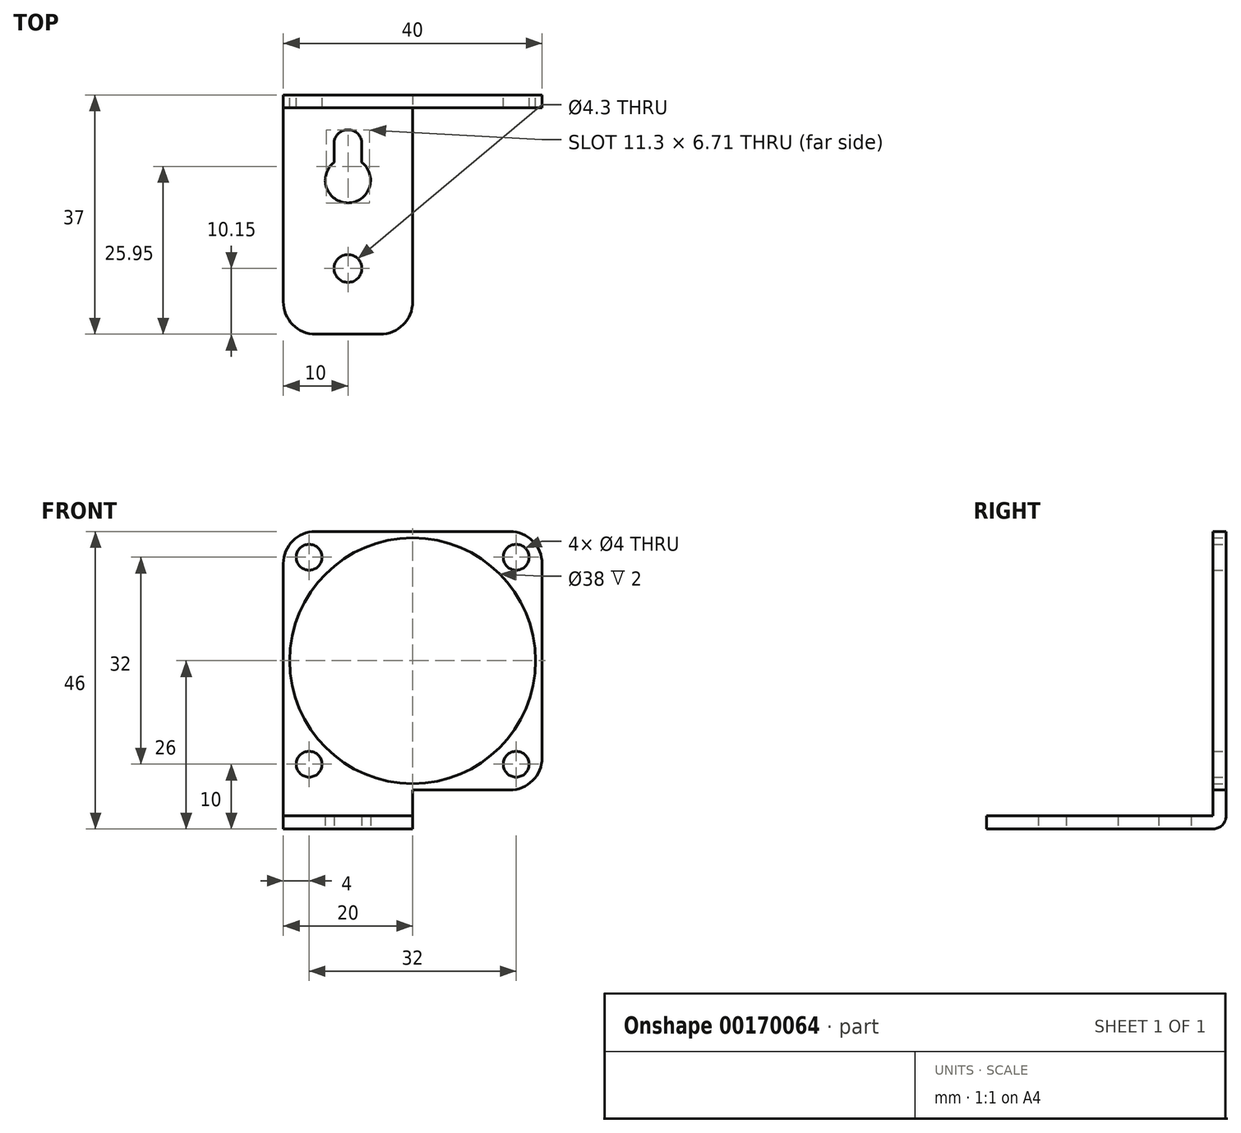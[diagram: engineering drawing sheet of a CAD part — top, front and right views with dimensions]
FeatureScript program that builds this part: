
annotation { "Feature Type Name" : "Feature", "Feature Type Description" : "" }
export const myFeature = defineFeature(function(context is Context, id is Id, definition is map)
    precondition{}
    {
        {
            var Q0;
            Q0=qCreatedBy(makeId("Front.planeOp"),FACE);
            var sketch = newSketch(context, id + "F0", { "sketchPlane" : qUnion([Q0])});
            skLineSegment(sketch, "E0.bottom", {"start": v(20, -20) * mm, "end": v(-20, -20) * mm});
            skLineSegment(sketch, "E0.top", {"start": v(20, 20) * mm, "end": v(-20, 20) * mm});
            skLineSegment(sketch, "E0.left", {"start": v(20, -20) * mm, "end": v(20, 20) * mm});
            skLineSegment(sketch, "E0.right", {"start": v(-20, -20) * mm, "end": v(-20, 20) * mm});
            skPoint(sketch, "E0.middle", {"position": v(0, 0) * mm});
            skCircle(sketch, "E1", {"center": v(16, 16) * mm, "radius": 2 * mm});
            skCircle(sketch, "E2", {"center": v(0, 0) * mm, "radius": 19 * mm});
            skCircle(sketch, "E3", {"center": v(-16, 16) * mm, "radius": 2 * mm});
            skCircle(sketch, "E4", {"center": v(16, -16) * mm, "radius": 2 * mm});
            skCircle(sketch, "E5", {"center": v(-16, -16) * mm, "radius": 2 * mm});
            skSolve(sketch);
        }
        {
            var Q0;
            Q0 = qSketchRegion(id + "F0", true);
            extrude(context, id + "F1", {"entities" : qUnion([Q0]), "depth" : 2 * mm});
        }
        {
            var Q0;
            Q0=makeQuery(id+"F1.opExtrude","SWEPT_FACE",FACE,{"disambiguationData":[OSD([sQuery(id+"F0.wireOp",EDGE,"E0.bottom")])]});
            var sketch = newSketch(context, id + "F2", { "sketchPlane" : qUnion([Q0])});
            skLineSegment(sketch, "E6.bottom", {"start": v(-20, 0) * mm, "end": v(0, 0) * mm});
            skLineSegment(sketch, "E6.top", {"start": v(-20, 2) * mm, "end": v(0, 2) * mm});
            skLineSegment(sketch, "E6.left", {"start": v(-20, 0) * mm, "end": v(-20, 2) * mm});
            skLineSegment(sketch, "E6.right", {"start": v(0, 0) * mm, "end": v(0, 2) * mm});
            skSolve(sketch);
        }
        {
            var Q0;
            Q0 = qSketchRegion(id + "F2", true);
            extrude(context, id + "F3", {"entities" : qUnion([Q0]), "operationType" : NewBodyOperationType.ADD, "depth" : 6 * mm});
        }
        {
            var Q0;
            Q0=makeQuery(id+"F3.opExtrude","CAP_FACE",FACE,{"disambiguationData":[OSD([sQuery(id+"F2.wireOp",EDGE,"E6.bottom"),sQuery(id+"F2.wireOp",EDGE,"E6.top"),sQuery(id+"F2.wireOp",EDGE,"E6.left"),sQuery(id+"F2.wireOp",EDGE,"E6.right")])],"isStart":false});
            var sketch = newSketch(context, id + "F4", { "sketchPlane" : qUnion([Q0])});
            skLineSegment(sketch, "E7.bottom", {"start": v(-20, 0) * mm, "end": v(0, 0) * mm});
            skLineSegment(sketch, "E7.top", {"start": v(-20, 37) * mm, "end": v(0, 37) * mm});
            skLineSegment(sketch, "E7.left", {"start": v(-20, 0) * mm, "end": v(-20, 37) * mm});
            skLineSegment(sketch, "E7.right", {"start": v(0, 0) * mm, "end": v(0, 37) * mm});
            skSolve(sketch);
        }
        {
            var Q0;
            Q0 = qSketchRegion(id + "F4", true);
            extrude(context, id + "F5", {"entities" : qUnion([Q0]), "operationType" : NewBodyOperationType.ADD, "oppositeDirection" : true, "depth" : 2 * mm});
        }
        {
            var Q0;
            Q0=makeQuery(id+"F1.opExtrude","SWEPT_EDGE",EDGE,{"disambiguationData":[OSD([sQuery(id+"F0.wireOp",EDGE,"E0.bottom"),sQuery(id+"F0.wireOp",EDGE,"E0.left")])]});
            var Q1;
            Q1=makeQuery(id+"F1.opExtrude","SWEPT_EDGE",EDGE,{"disambiguationData":[OSD([sQuery(id+"F0.wireOp",EDGE,"E0.top"),sQuery(id+"F0.wireOp",EDGE,"E0.left")])]});
            var Q2;
            Q2=makeQuery(id+"F1.opExtrude","SWEPT_EDGE",EDGE,{"disambiguationData":[OSD([sQuery(id+"F0.wireOp",EDGE,"E0.top"),sQuery(id+"F0.wireOp",EDGE,"E0.right")])]});
            var Q3;
            Q3=makeQuery(id+"F5.opExtrude","SWEPT_EDGE",EDGE,{"disambiguationData":[OSD([sQuery(id+"F4.wireOp",EDGE,"E7.top"),sQuery(id+"F4.wireOp",EDGE,"E7.left")])]});
            var Q4;
            Q4=makeQuery(id+"F5.opExtrude","SWEPT_EDGE",EDGE,{"disambiguationData":[OSD([sQuery(id+"F4.wireOp",EDGE,"E7.top"),sQuery(id+"F4.wireOp",EDGE,"E7.right")])]});
            fillet(context, id + "F6", {"entities" : qUnion([Q0, Q1, Q2, Q3, Q4]), "radius" : 5 * mm, "tangentPropagation" : true, "allowEdgeOverflow" : false});
        }
        {
            var Q0;
            Q0=makeQuery(id+"F5.boolean.opBoolean","MERGE",FACE,{"derivedFrom":[makeQuery(id+"F3.opExtrude","CAP_FACE",FACE,{"disambiguationData":[OSD([sQuery(id+"F2.wireOp",EDGE,"E6.bottom"),sQuery(id+"F2.wireOp",EDGE,"E6.top"),sQuery(id+"F2.wireOp",EDGE,"E6.left"),sQuery(id+"F2.wireOp",EDGE,"E6.right")])],"isStart":false}),makeQuery(id+"F5.opExtrude","CAP_FACE",FACE,{"disambiguationData":[OSD([sQuery(id+"F4.wireOp",EDGE,"E7.bottom"),sQuery(id+"F4.wireOp",EDGE,"E7.top"),sQuery(id+"F4.wireOp",EDGE,"E7.left"),sQuery(id+"F4.wireOp",EDGE,"E7.right")])],"isStart":true})]});
            var sketch = newSketch(context, id + "F7", { "sketchPlane" : qUnion([Q0])});
            skCircle(sketch, "E8", {"center": v(-10, 26.85) * mm, "radius": 2.15 * mm});
            skPoint(sketch, "E8.centerSnap0", {"position": v(-10, 37) * mm});
            skArc(sketch, "E9", {"start": v(-12.15, 7.55) * mm, "mid": v(-10, 5.4) * mm, "end": v(-7.85, 7.55) * mm});
            skArc(sketch, "E10", {"start": v(-7.85, 10.44) * mm, "mid": v(-10, 16.7) * mm, "end": v(-12.15, 10.44) * mm});
            skLineSegment(sketch, "E11", {"start": v(-12.15, 7.55) * mm, "end": v(-12.15, 10.44) * mm});
            skLineSegment(sketch, "E12", {"start": v(-7.85, 7.55) * mm, "end": v(-7.85, 10.44) * mm});
            skSolve(sketch);
        }
        {
            var Q0;
            Q0 = qSketchRegion(id + "F7", true);
            extrude(context, id + "F8", {"entities" : qUnion([Q0]), "operationType" : NewBodyOperationType.REMOVE, "oppositeDirection" : true, "depth" : 3 * mm});
        }
        {
            var Q0;
            Q0=makeQuery(id+"F3.opExtrude","CAP_EDGE",EDGE,{"disambiguationData":[OSD([sQuery(id+"F2.wireOp",EDGE,"E6.right")])],"isStart":true});
            var Q1;
            Q1=makeQuery(id+"F3.opExtrude","CAP_EDGE",EDGE,{"disambiguationData":[OSD([sQuery(id+"F2.wireOp",EDGE,"E6.bottom")])],"isStart":false});
            fillet(context, id + "F9", {"entities" : qUnion([Q0, Q1]), "radius" : 2 * mm, "tangentPropagation" : true, "allowEdgeOverflow" : false});
        }
    });
